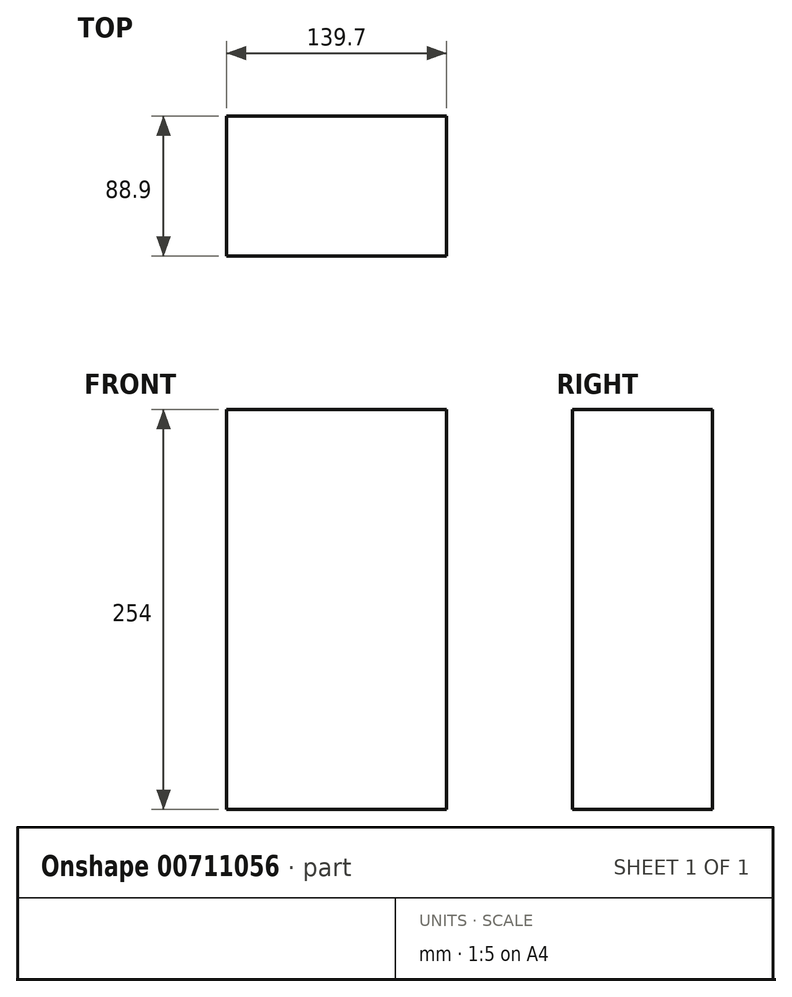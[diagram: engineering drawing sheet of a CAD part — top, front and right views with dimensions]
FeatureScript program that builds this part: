
annotation { "Feature Type Name" : "Feature", "Feature Type Description" : "" }
export const myFeature = defineFeature(function(context is Context, id is Id, definition is map)
    precondition{}
    {
        {
            var Q0;
            Q0=qCreatedBy(makeId("Top.planeOp"),FACE);
            var sketch = newSketch(context, id + "F0", { "sketchPlane" : qUnion([Q0])});
            skLineSegment(sketch, "E0.bottom", {"start": v(73, 44.45) * mm, "end": v(-66.7, 44.45) * mm});
            skLineSegment(sketch, "E0.top", {"start": v(73, -44.45) * mm, "end": v(-66.7, -44.45) * mm});
            skLineSegment(sketch, "E0.left", {"start": v(73, 44.45) * mm, "end": v(73, -44.45) * mm});
            skLineSegment(sketch, "E0.right", {"start": v(-66.7, 44.45) * mm, "end": v(-66.7, -44.45) * mm});
            skPoint(sketch, "E0.middle", {"position": v(3.15, 0) * mm});
            skSolve(sketch);
        }
        {
            var Q0;
            Q0 = qSketchRegion(id + "F0", true);
            extrude(context, id + "F1", {"entities" : qUnion([Q0]), "depth" : 254 * mm, "offsetDistance" : 25.4 * mm});
        }
    });
